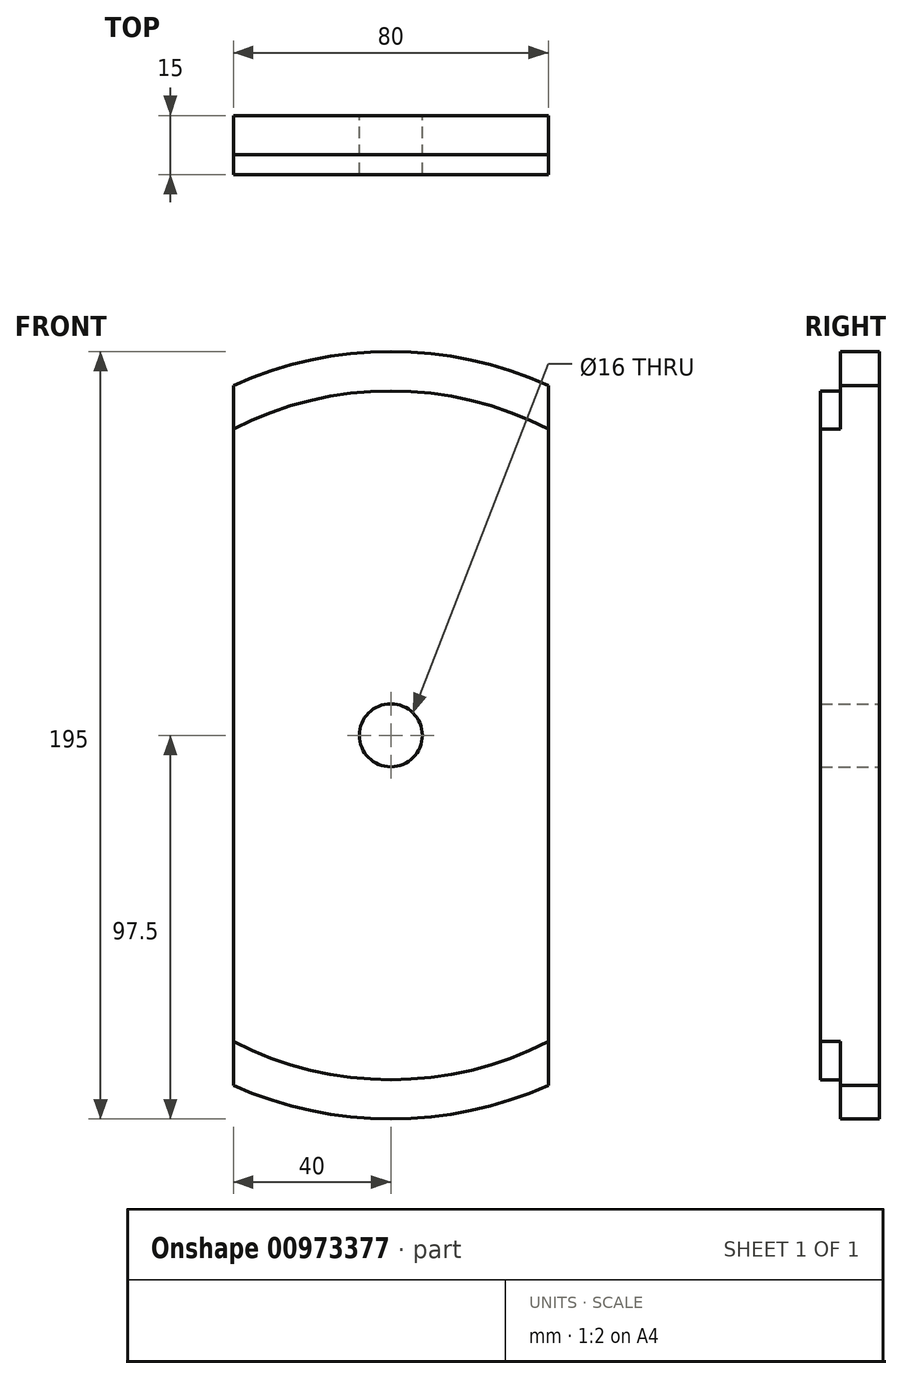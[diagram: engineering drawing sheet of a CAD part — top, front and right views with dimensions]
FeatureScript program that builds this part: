
annotation { "Feature Type Name" : "Feature", "Feature Type Description" : "" }
export const myFeature = defineFeature(function(context is Context, id is Id, definition is map)
    precondition{}
    {
        {
            var Q0;
            Q0=qCreatedBy(makeId("Front.planeOp"),FACE);
            var sketch = newSketch(context, id + "F0", { "sketchPlane" : qUnion([Q0])});
            skCircle(sketch, "E0", {"center": v(0, 0) * mm, "radius": 8 * mm});
            skCircle(sketch, "E1", {"center": v(0, 0) * mm, "radius": 87.5 * mm});
            skCircle(sketch, "E2", {"center": v(0, 0) * mm, "radius": 97.5 * mm});
            skLineSegment(sketch, "E3.bottom", {"start": v(-40, 99.5) * mm, "end": v(40, 99.5) * mm});
            skLineSegment(sketch, "E3.top", {"start": v(-40, -106.09) * mm, "end": v(40, -106.09) * mm});
            skLineSegment(sketch, "E3.left", {"start": v(-40, 99.5) * mm, "end": v(-40, -106.09) * mm});
            skLineSegment(sketch, "E3.right", {"start": v(40, 99.5) * mm, "end": v(40, -106.09) * mm});
            skSolve(sketch);
        }
        {
            var Q0;
            Q0=makeQuery(id+"F0.imprint","IMPRINT",FACE,{"disambiguationData":[TD([[makeQuery(id+"F0.imprint","IMPRINT",EDGE,{"derivedFrom":sQuery(id+"F0.wireOp",EDGE,"E0")}),-1.0]])]});
            extrude(context, id + "F1", {"entities" : qUnion([Q0]), "depth" : 15 * mm, "offsetDistance" : 25 * mm});
        }
        {
            var Q0;
            {var subQ0=sQuery(id+"F0.wireOp",EDGE,"E3.left");var subQ1=sQuery(id+"F0.wireOp",EDGE,"E1");var subQ2=makeQuery(id+"F0.imprint","INTERSECT",VERTEX,{"disambiguationData":[OD(0.0)],"derivedFrom":[subQ1,subQ0]});Q0=makeQuery(id+"F0.imprint","IMPRINT",FACE,{"disambiguationData":[TD([[makeQuery(id+"F0.imprint","IMPRINT",EDGE,{"disambiguationData":[TD([[subQ2,1.0]])],"derivedFrom":subQ1}),-1.0]])]});}
            var Q1;
            {var subQ0=sQuery(id+"F0.wireOp",EDGE,"E3.left");var subQ1=sQuery(id+"F0.wireOp",EDGE,"E1");var subQ2=makeQuery(id+"F0.imprint","INTERSECT",VERTEX,{"disambiguationData":[OD(1.0)],"derivedFrom":[subQ1,subQ0]});Q1=makeQuery(id+"F0.imprint","IMPRINT",FACE,{"disambiguationData":[TD([[makeQuery(id+"F0.imprint","IMPRINT",EDGE,{"disambiguationData":[TD([[subQ2,-1.0]])],"derivedFrom":subQ1}),-1.0]])]});}
            extrude(context, id + "F2", {"entities" : qUnion([Q0, Q1]), "operationType" : NewBodyOperationType.ADD, "depth" : 10 * mm, "offsetDistance" : 25 * mm});
        }
    });
